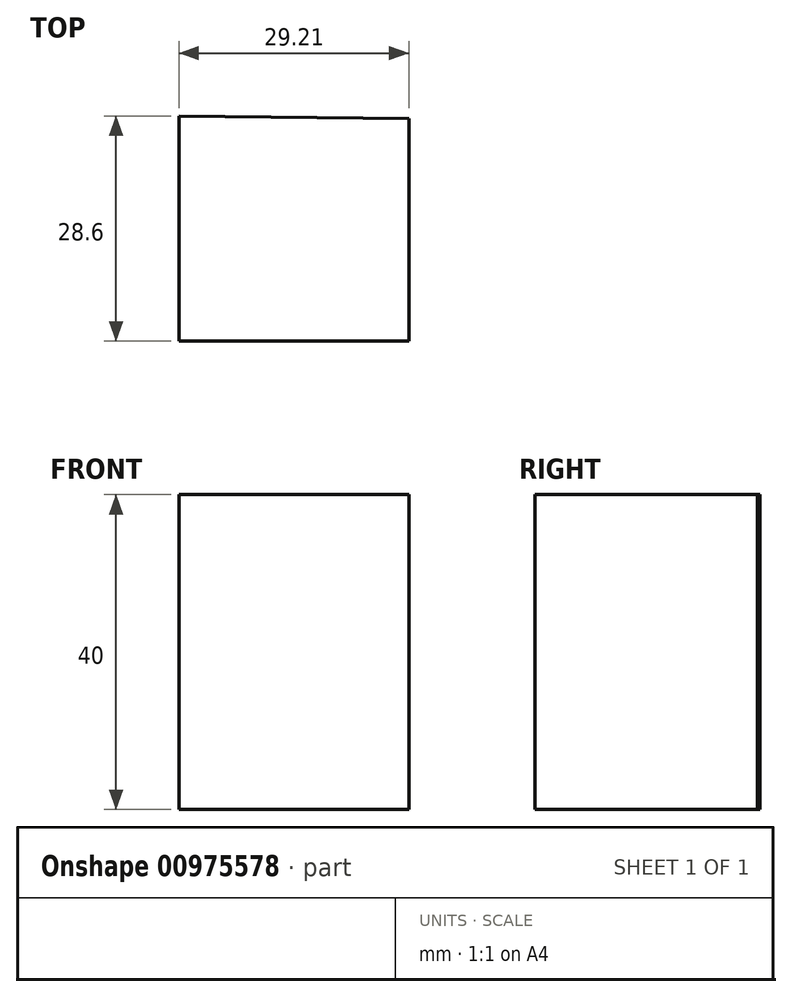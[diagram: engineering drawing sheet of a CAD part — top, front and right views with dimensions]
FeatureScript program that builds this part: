
annotation { "Feature Type Name" : "Feature", "Feature Type Description" : "" }
export const myFeature = defineFeature(function(context is Context, id is Id, definition is map)
    precondition{}
    {
        {
            var Q0;
            Q0=qCreatedBy(makeId("Top.planeOp"),FACE);
            var sketch = newSketch(context, id + "F0", { "sketchPlane" : qUnion([Q0])});
            skLineSegment(sketch, "E0", {"start": v(-19.16, 14.7) * mm, "end": v(-19.16, -13.9) * mm});
            skLineSegment(sketch, "E1", {"start": v(-19.16, -13.9) * mm, "end": v(10.05, -13.9) * mm});
            skLineSegment(sketch, "E2", {"start": v(10.05, -13.9) * mm, "end": v(10.05, 14.4) * mm});
            skLineSegment(sketch, "E3", {"start": v(10.05, 14.4) * mm, "end": v(-19.16, 14.7) * mm});
            skSolve(sketch);
        }
        {
            var Q0;
            Q0 = qSketchRegion(id + "F0", true);
            extrude(context, id + "F1", {"entities" : qUnion([Q0]), "depth" : 40 * mm, "offsetDistance" : 25 * mm});
        }
    });
